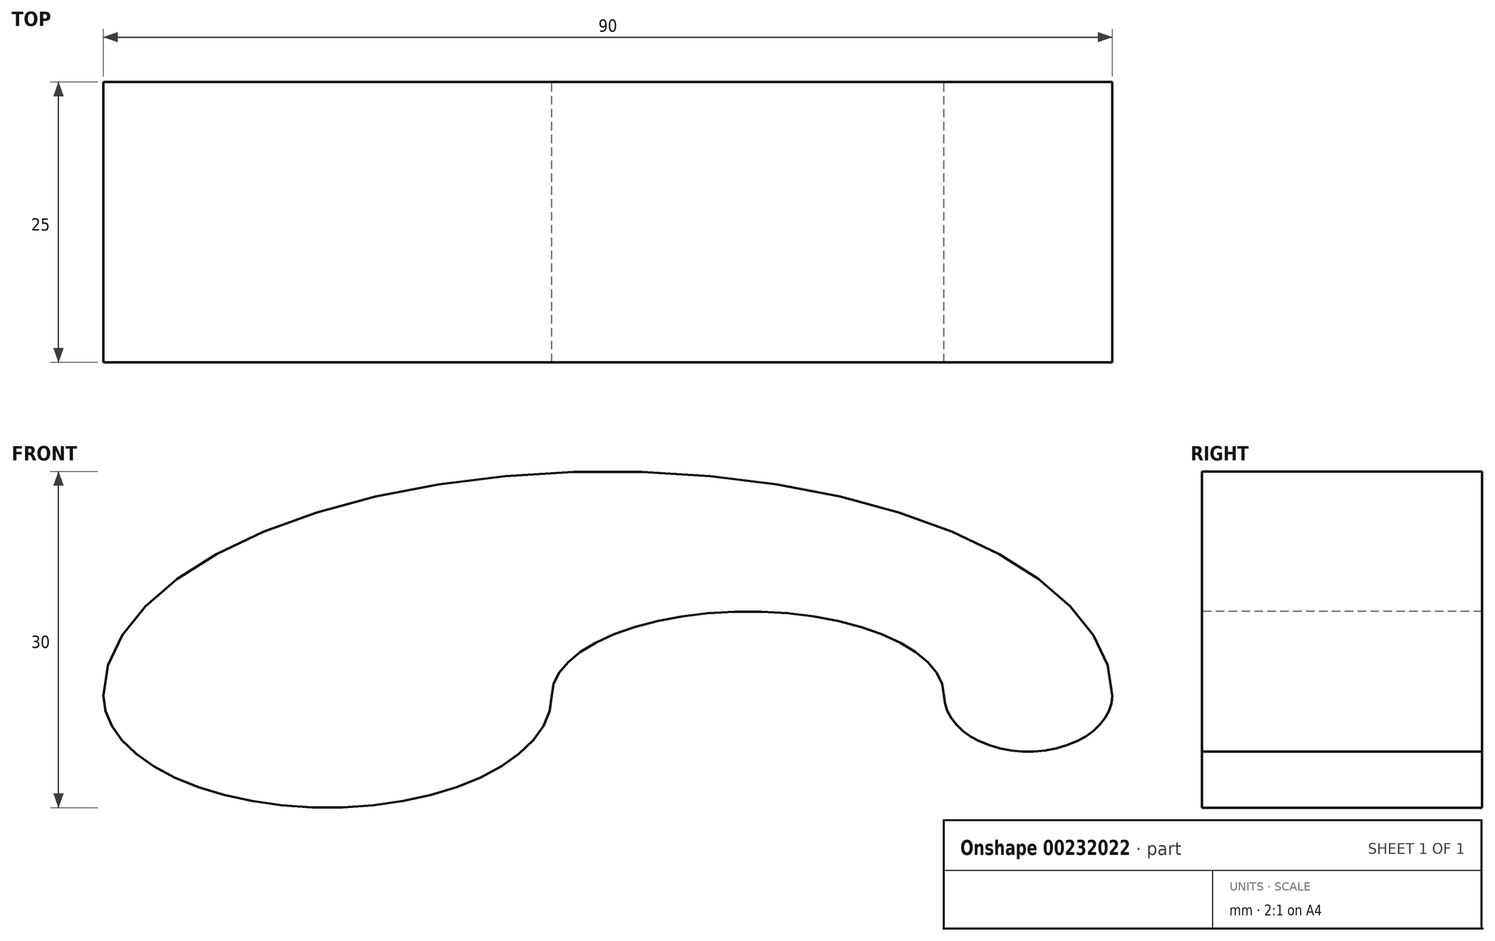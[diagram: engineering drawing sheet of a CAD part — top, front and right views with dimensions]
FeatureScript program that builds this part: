
annotation { "Feature Type Name" : "Feature", "Feature Type Description" : "" }
export const myFeature = defineFeature(function(context is Context, id is Id, definition is map)
    precondition{}
    {
        {
            var Q0;
            Q0=qCreatedBy(makeId("Front.planeOp"),FACE);
            var sketch = newSketch(context, id + "F0", { "sketchPlane" : qUnion([Q0])});
            skEllipticalArc(sketch, "E0", {});
            skEllipticalArc(sketch, "E1", {});
            skEllipticalArc(sketch, "E2", {});
            skEllipticalArc(sketch, "E3", {});
            const initialGuessF0  = {"E0": [0, 0, -1, 0, 0.045, 0.02, 3.141592653589793, 0], "E1": [-0.025, 0, -1, 0, 0.02, 0.01, 0, 3.141592653589793], "E2": [0.0125, 0, -1, 0, 0.0175, 0.0075, 3.141592653589793, 0], "E3": [0.0375, 0, -1, 0, 0.0075, 0.005, 0, 3.141592653589793]};
            skSetInitialGuess(sketch, initialGuessF0);
            skSolve(sketch);
        }
        {
            var Q0;
            Q0=makeQuery(id+"F0.imprint","IMPRINT",FACE,{"disambiguationData":[TD([[makeQuery(id+"F0.imprint","IMPRINT",EDGE,{"derivedFrom":sQuery(id+"F0.wireOp",EDGE,"E0")}),1.0]])]});
            extrude(context, id + "F1", {"entities" : qUnion([Q0]), "depth" : 25 * mm});
        }
    });
